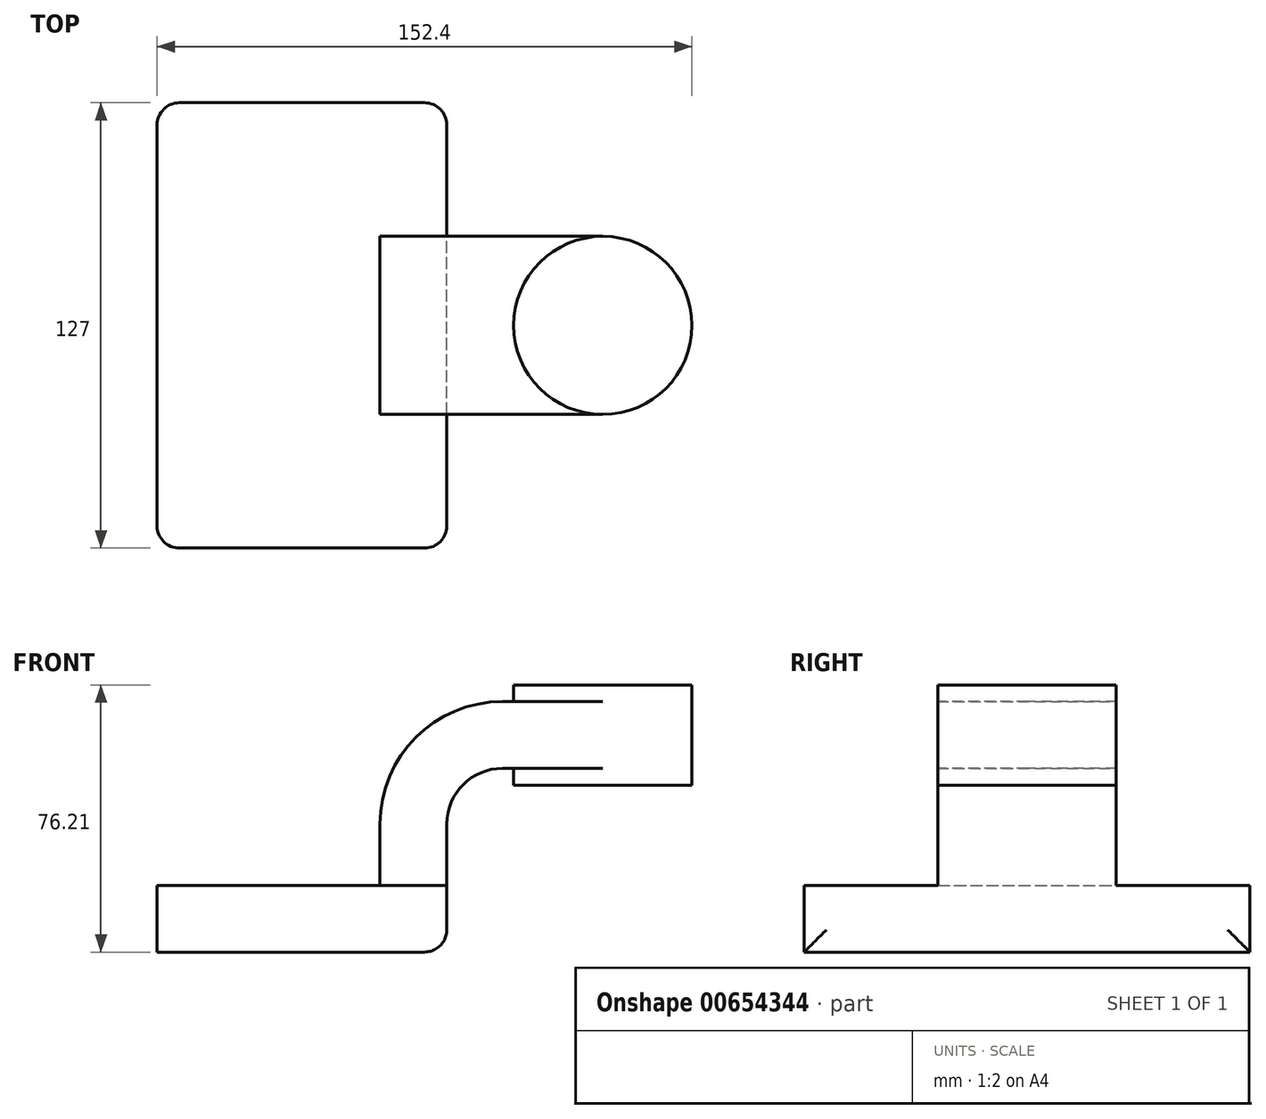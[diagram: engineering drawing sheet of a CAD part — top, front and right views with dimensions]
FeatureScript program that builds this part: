
annotation { "Feature Type Name" : "Feature", "Feature Type Description" : "" }
export const myFeature = defineFeature(function(context is Context, id is Id, definition is map)
    precondition{}
    {
        {
            var Q0;
            Q0=qCreatedBy(makeId("Front.planeOp"),FACE);
            var sketch = newSketch(context, id + "F0", { "sketchPlane" : qUnion([Q0])});
            skLineSegment(sketch, "E0.bottom", {"start": v(-41.27, -9.53) * mm, "end": v(41.28, -9.53) * mm});
            skLineSegment(sketch, "E0.top", {"start": v(-41.28, 9.53) * mm, "end": v(41.28, 9.53) * mm});
            skLineSegment(sketch, "E0.left", {"start": v(-41.28, -9.53) * mm, "end": v(-41.28, 9.53) * mm});
            skLineSegment(sketch, "E0.right", {"start": v(41.28, -9.53) * mm, "end": v(41.28, 9.52) * mm});
            skPoint(sketch, "E0.middle", {"position": v(0, 0) * mm});
            skLineSegment(sketch, "E1.bottom", {"start": v(60.33, 38.1) * mm, "end": v(111.12, 38.1) * mm});
            skLineSegment(sketch, "E1.top", {"start": v(60.32, 66.67) * mm, "end": v(111.12, 66.67) * mm});
            skLineSegment(sketch, "E1.left", {"start": v(60.33, 38.1) * mm, "end": v(60.32, 66.67) * mm});
            skLineSegment(sketch, "E1.right", {"start": v(111.12, 38.1) * mm, "end": v(111.12, 66.67) * mm});
            skPoint(sketch, "E1.middle", {"position": v(85.72, 52.39) * mm});
            skLineSegment(sketch, "E2", {"start": v(41.28, 9.52) * mm, "end": v(41.28, 27) * mm});
            skArc(sketch, "E3", {"start": v(41.27, 27) * mm, "mid": v(45.92, 38.23) * mm, "end": v(57.15, 42.88) * mm});
            skLineSegment(sketch, "E4", {"start": v(57.15, 42.88) * mm, "end": v(85.72, 42.88) * mm});
            skLineSegment(sketch, "E5.0", {"start": v(57.15, 61.93) * mm, "end": v(85.72, 61.93) * mm});
            skArc(sketch, "E5.1", {"start": v(22.23, 27) * mm, "mid": v(32.45, 51.7) * mm, "end": v(57.15, 61.93) * mm});
            skLineSegment(sketch, "E5.2", {"start": v(22.23, 9.52) * mm, "end": v(22.23, 27) * mm});
            skLineSegment(sketch, "E6", {"start": v(85.72, 38.1) * mm, "end": v(85.72, 66.67) * mm});
            skFitSpline(sketch, "E7", {"points": [v(-41.28, 9.53) * mm, v(57.15, 61.93) * mm], "startDerivative": vector(0.48, 81.86) * mm, "endDerivative": vector(150.52, -2.14) * mm});
            skSolve(sketch);
        }
        {
            var Q0;
            Q0=makeQuery(id+"F0.imprint","IMPRINT",FACE,{"disambiguationData":[TD([[makeQuery(id+"F0.imprint","IMPRINT",EDGE,{"derivedFrom":sQuery(id+"F0.wireOp",EDGE,"E0.bottom")}),1.0]])]});
            extrude(context, id + "F1", {"entities" : qUnion([Q0]), "depth" : 127 * mm, "offsetDistance" : 25.4 * mm, "symmetric" : true});
        }
        {
            var Q0;
            {var subQ1=sQuery(id+"F0.wireOp",EDGE,"E2");Q0=makeQuery(id+"F0.imprint","IMPRINT",FACE,{"disambiguationData":[TD([[makeQuery(id+"F0.imprint","IMPRINT",EDGE,{"derivedFrom":subQ1}),1.0]])]});}
            var Q1;
            {var subQ0=sQuery(id+"F0.wireOp",EDGE,"E4");var subQ1=sQuery(id+"F0.wireOp",EDGE,"E1.left");var subQ2=makeQuery(id+"F0.imprint","INTERSECT",VERTEX,{"derivedFrom":[subQ1,subQ0]});Q1=makeQuery(id+"F0.imprint","IMPRINT",FACE,{"disambiguationData":[TD([[makeQuery(id+"F0.imprint","IMPRINT",EDGE,{"disambiguationData":[TD([[subQ2,-1.0]])],"derivedFrom":subQ1}),-1.0]])]});}
            extrude(context, id + "F2", {"entities" : qUnion([Q0, Q1]), "operationType" : NewBodyOperationType.ADD, "depth" : 50.8 * mm, "offsetDistance" : 25.4 * mm, "symmetric" : true});
        }
        {
            var Q0;
            Q0=makeQuery(id+"F0.imprint","IMPRINT",FACE,{"disambiguationData":[TD([[makeQuery(id+"F0.imprint","IMPRINT",EDGE,{"derivedFrom":sQuery(id+"F0.wireOp",EDGE,"E5.1")}),1.0]])]});
            extrude(context, id + "F3", {"entities" : qUnion([Q0]), "operationType" : NewBodyOperationType.ADD, "depth" : 15.88 * mm, "offsetDistance" : 25.4 * mm, "symmetric" : true});
        }
        {
            var Q0;
            {var subQ0=sQuery(id+"F0.wireOp",EDGE,"E1.right");Q0=makeQuery(id+"F0.imprint","IMPRINT",FACE,{"disambiguationData":[TD([[makeQuery(id+"F0.imprint","IMPRINT",EDGE,{"derivedFrom":subQ0}),1.0]])]});}
            var Q1;
            Q1=sQuery(id+"F0.wireOp",EDGE,"E6");
            revolve(context, id + "F4", {"operationType" : NewBodyOperationType.ADD, "entities" : qUnion([Q0]), "axis" : qUnion([Q1]), "revolveType" : RevolveType.FULL});
        }
        {
            var Q0;
            Q0=makeQuery(id+"F1.opExtrude","CAP_EDGE",EDGE,{"disambiguationData":[OSD([sQuery(id+"F0.wireOp",EDGE,"E0.left")])],"isStart":false});
            var Q1;
            Q1=makeQuery(id+"F1.opExtrude","CAP_EDGE",EDGE,{"disambiguationData":[OSD([sQuery(id+"F0.wireOp",EDGE,"E0.right")])],"isStart":false});
            var Q2;
            Q2=makeQuery(id+"F1.opExtrude","CAP_EDGE",EDGE,{"disambiguationData":[OSD([sQuery(id+"F0.wireOp",EDGE,"E0.right")])],"isStart":true});
            var Q3;
            Q3=makeQuery(id+"F1.opExtrude","SWEPT_EDGE",EDGE,{"disambiguationData":[OSD([sQuery(id+"F0.wireOp",EDGE,"E0.bottom"),sQuery(id+"F0.wireOp",EDGE,"E0.right")])]});
            var Q4;
            Q4=makeQuery(id+"F1.opExtrude","CAP_EDGE",EDGE,{"disambiguationData":[OSD([sQuery(id+"F0.wireOp",EDGE,"E0.left")])],"isStart":true});
            fillet(context, id + "F5", {"entities" : qUnion([Q0, Q1, Q2, Q3, Q4]), "radius" : 6.35 * mm, "tangentPropagation" : true, "allowEdgeOverflow" : false});
        }
    });
